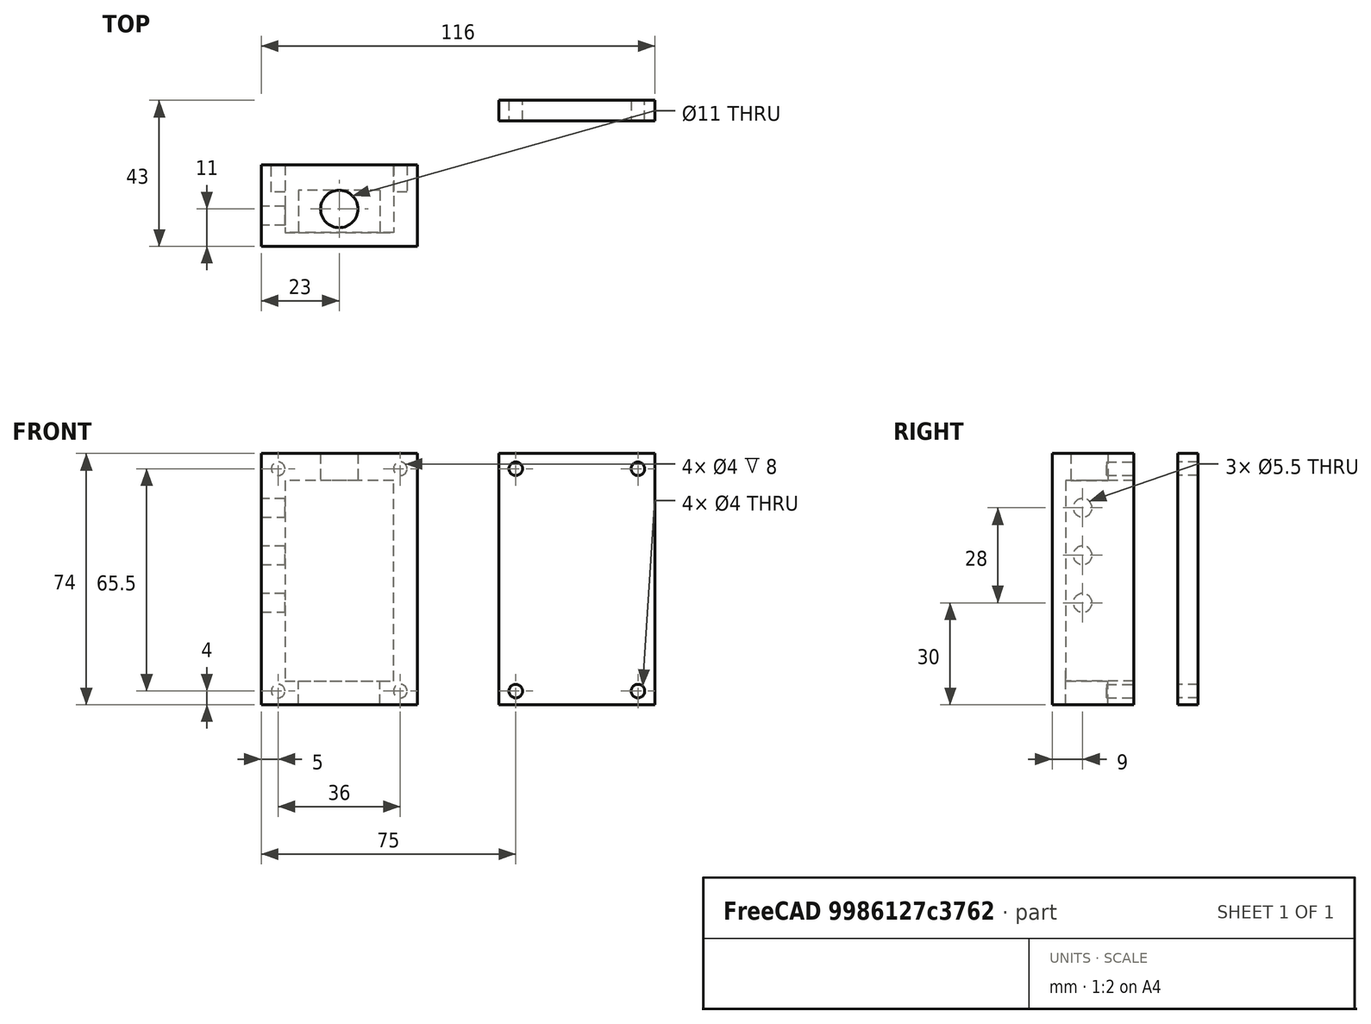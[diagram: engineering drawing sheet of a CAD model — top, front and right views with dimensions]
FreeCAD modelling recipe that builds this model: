
FCSTD DOCUMENT  (FreeCAD 0.20R29603 (Git))
Label: Reciever Housing
License: All rights reserved
LicenseURL: http://en.wikipedia.org/wiki/All_rights_reserved
objects: Sketcher::SketchObject×8, PartDesign::Pocket×5, PartDesign::Pad×2, PartDesign::Hole×2, Mesh::Feature×2, PartDesign::Body×2
note: 28 computed .brp shape members not serialized (recipe doc carries the construction recipe); baked Part::Feature solids carry a one-line shape summary decoded from their .brp

FEATURE [Sketcher::SketchObject] Sketch
  FullyConstrained = true
  MapMode = 5
  Placement = pos=(0,0,0) rot=(1,0,0;1.5708rad)
  Support = -> [XZ_Plane]
  sketch-geometry (4):
    g0: LineSegment StartX=-23 StartY=40 StartZ=0 EndX=23 EndY=40 EndZ=0
    g1: LineSegment StartX=23 StartY=40 StartZ=0 EndX=23 EndY=-34 EndZ=0
    g2: LineSegment StartX=23 StartY=-34 StartZ=0 EndX=-23 EndY=-34 EndZ=0
    g3: LineSegment StartX=-23 StartY=-34 StartZ=0 EndX=-23 EndY=40 EndZ=0
  constraints (12):
    c: Horizontal(g0)
    c: Vertical(g1)
    c: Horizontal(g2)
    c: Coincident(g1,g0)
    c: Coincident(g0,g3)
    c: Coincident(g1,g2)
    c: Coincident(g2,g3)
    c: DistanceX(g0,g0) = 46
    c: DistanceY(g1,g0) = 74
    c: DistanceX(g2,g1) = 46
    c: DistanceX(g-1,g1) = 23
    c: DistanceY(g1,g-1) = 34
FEATURE [PartDesign::Pad] Pad
  Direction = (0,-1,-2e-16)
  Length = 24
  Length2 = 10
  Placement = pos=(0,0,0) rot=(1,0,0;1.5708rad)
  Profile = -> Sketch
  ReferenceAxis = -> Sketch [N_Axis]
  Type = 0
FEATURE [Sketcher::SketchObject] Sketch001
  FullyConstrained = true
  MapMode = 5
  Placement = pos=(0,0,0) rot=(-1,0,0;1.5708rad)
  Support = -> [Pad]
  sketch-geometry (4):
    g0: LineSegment StartX=-16 StartY=27 StartZ=0 EndX=16 EndY=27 EndZ=0
    g1: LineSegment StartX=16 StartY=27 StartZ=0 EndX=16 EndY=-32 EndZ=0
    g2: LineSegment StartX=16 StartY=-32 StartZ=0 EndX=-16 EndY=-32 EndZ=0
    g3: LineSegment StartX=-16 StartY=-32 StartZ=0 EndX=-16 EndY=27 EndZ=0
  constraints (12):
    c: Horizontal(g0)
    c: Vertical(g1)
    c: Horizontal(g2)
    c: Vertical(g3)
    c: Coincident(g1,g0)
    c: Coincident(g0,g3)
    c: Coincident(g3,g2)
    c: Coincident(g1,g2)
    c: DistanceX(g0,g-1) = 16
    c: DistanceY(g-1,g0) = 27
    c: DistanceX(g0,g0) = 32
    c: DistanceY(g1,g0) = 59
FEATURE [PartDesign::Pocket] Pocket
  BaseFeature = -> Pad
  Direction = (0,-1,-2e-16)
  Length = 20
  Length2 = 5
  Placement = pos=(0,0,0) rot=(1,0,0;1.5708rad)
  Profile = -> Sketch001
  ReferenceAxis = -> Sketch001 [N_Axis]
  Type = 0
FEATURE [Sketcher::SketchObject] Sketch002  label="Power plug hole"
  FullyConstrained = true
  MapMode = 5
  Placement = pos=(0,0,40) rot=(0,0,1;3.14159rad)
  Support = -> [Pocket]
  sketch-geometry (1):
    g0: Circle CenterX=0 CenterY=13 CenterZ=0 NormalX=0 NormalY=0 NormalZ=1 AngleXU=0 Radius=5.5
  constraints (3):
    c: Diameter(g0) = 11
    c: DistanceX(g0,g-1) = 0
    c: DistanceY(g-1,g0) = 13
FEATURE [PartDesign::Hole] Hole
  BaseFeature = -> Pocket
  CustomThreadClearance = 0
  Depth = 25
  DepthType = 0
  Diameter = 6
  DrillForDepth = false
  DrillPoint = 1
  DrillPointAngle = 118
  HoleCutCountersinkAngle = 90
  HoleCutCustomValues = false
  HoleCutDepth = 0
  HoleCutDiameter = 6.1
  HoleCutType = 0
  ModelThread = false
  Placement = pos=(0,0,0) rot=(1,0,0;1.5708rad)
  Profile = -> Pocket [Face1]
  Tapered = false
  TaperedAngle = 90
  ThreadClass = 0
  ThreadDepth = 25
  ThreadDepthType = 0
  ThreadDirection = 0
  ThreadFit = 0
  ThreadSize = 0
  ThreadType = 0
  Threaded = false
  UseCustomThreadClearance = false
FEATURE [PartDesign::Hole] Hole001
  BaseFeature = -> Hole
  CustomThreadClearance = 0
  Depth = 25
  DepthType = 0
  Diameter = 11
  DrillForDepth = false
  DrillPoint = 1
  DrillPointAngle = 118
  HoleCutCountersinkAngle = 90
  HoleCutCustomValues = false
  HoleCutDepth = 0
  HoleCutDiameter = 6.1
  HoleCutType = 0
  ModelThread = false
  Placement = pos=(0,0,0) rot=(1,0,0;1.5708rad)
  Profile = -> Sketch002
  Tapered = false
  TaperedAngle = 90
  ThreadClass = 0
  ThreadDepth = 25
  ThreadDepthType = 0
  ThreadDirection = 0
  ThreadFit = 0
  ThreadSize = 0
  ThreadType = 0
  Threaded = false
  UseCustomThreadClearance = false
FEATURE [Mesh::Feature] JST_Female_3pin  label="JST Female 3pin"
  Placement = pos=(2e-16,-14,-47) rot=(0,-0.707107,0.707107;3.14159rad)
FEATURE [Sketcher::SketchObject] Sketch003  label="JST Connector Hole"
  FullyConstrained = true
  MapMode = 5
  Placement = pos=(0,0,-34) rot=(1,0,0;3.14159rad)
  Support = -> [Hole001]
  sketch-geometry (4):
    g0: LineSegment StartX=-12 StartY=20 StartZ=0 EndX=12 EndY=20 EndZ=0
    g1: LineSegment StartX=12 StartY=7.5 StartZ=0 EndX=12 EndY=20 EndZ=0
    g2: LineSegment StartX=12 StartY=7.5 StartZ=0 EndX=-12 EndY=7.5 EndZ=0
    g3: LineSegment StartX=-12 StartY=7.5 StartZ=0 EndX=-12 EndY=20 EndZ=0
  constraints (12):
    c: Horizontal(g0)
    c: Vertical(g1)
    c: Horizontal(g2)
    c: Vertical(g3)
    c: Coincident(g3,g0)
    c: Coincident(g0,g1)
    c: Coincident(g1,g2)
    c: Coincident(g2,g3)
    c: DistanceX(g-1,g1) = 12
    c: DistanceX(g2,g-1) = 12
    c: DistanceY(g2,g0) = 12.5
    c: DistanceY(g-1,g2) = 7.5
FEATURE [PartDesign::Pocket] Pocket001
  BaseFeature = -> Hole001
  Direction = (0,3e-16,1)
  Length = 10
  Length2 = 5
  Placement = pos=(0,0,0) rot=(1,0,0;1.5708rad)
  Profile = -> Sketch003
  ReferenceAxis = -> Sketch003 [N_Axis]
  Type = 0
FEATURE [Sketcher::SketchObject] Sketch004  label="Top"
  FullyConstrained = true
  MapMode = 5
  Placement = pos=(0,0,0) rot=(1,0,0;1.5708rad)
  Support = -> [XZ_Plane001]
  sketch-geometry (4):
    g0: LineSegment StartX=23 StartY=-34 StartZ=0 EndX=-23 EndY=-34 EndZ=0
    g1: LineSegment StartX=-23 StartY=-34 StartZ=0 EndX=-23 EndY=40 EndZ=0
    g2: LineSegment StartX=-23 StartY=40 StartZ=0 EndX=23 EndY=40 EndZ=0
    g3: LineSegment StartX=23 StartY=40 StartZ=0 EndX=23 EndY=-34 EndZ=0
  constraints (12):
    c: Horizontal(g0)
    c: Vertical(g1)
    c: Horizontal(g2)
    c: Vertical(g3)
    c: Coincident(g1,g2)
    c: Coincident(g3,g2)
    c: Coincident(g3,g0)
    c: Coincident(g1,g0)
    c: DistanceY(g0,g1) = 74
    c: DistanceX(g1,g2) = 46
    c: DistanceX(g0,g-1) = 23
    c: DistanceY(g0,g-1) = 34
FEATURE [PartDesign::Pad] Pad001
  Direction = (0,-1,-2e-16)
  Length = 6
  Length2 = 10
  Placement = pos=(0,0,0) rot=(1,0,0;1.5708rad)
  Profile = -> Sketch004
  ReferenceAxis = -> Sketch004 [N_Axis]
  Type = 0
FEATURE [Sketcher::SketchObject] Sketch005  label="TopMount Holes1"
  FullyConstrained = true
  MapMode = 5
  Placement = pos=(0,0,0) rot=(-1,0,0;1.5708rad)
  Support = -> [Pocket001]
  sketch-geometry (4):
    g0: Circle CenterX=18 CenterY=-35.5 CenterZ=0 NormalX=0 NormalY=0 NormalZ=1 AngleXU=0 Radius=2
    g1: Circle CenterX=-18 CenterY=-35.5 CenterZ=0 NormalX=0 NormalY=0 NormalZ=1 AngleXU=0 Radius=2
    g2: Circle CenterX=-18 CenterY=30 CenterZ=0 NormalX=0 NormalY=0 NormalZ=1 AngleXU=0 Radius=2
    g3: Circle CenterX=18 CenterY=30 CenterZ=0 NormalX=0 NormalY=0 NormalZ=1 AngleXU=0 Radius=2
  constraints (12):
    c: DistanceX(g-1,g0) = 18
    c: DistanceY(g0,g-1) = 35.5
    c: Diameter(g0) = 4
    c: DistanceY(g1,g-1) = 35.5
    c: DistanceX(g1,g-1) = 18
    c: Diameter(g1) = 4
    c: DistanceX(g2,g-1) = 18
    c: DistanceY(g-1,g2) = 30
    c: Diameter(g2) = 4
    c: DistanceX(g-1,g3) = 18
    c: DistanceY(g-1,g3) = 30
    c: Diameter(g3) = 4
FEATURE [PartDesign::Pocket] Pocket002
  BaseFeature = -> Pocket001
  Direction = (0,-1,2e-16)
  Length = 8
  Length2 = 5
  Placement = pos=(0,0,0) rot=(1,0,0;1.5708rad)
  Profile = -> Sketch005
  ReferenceAxis = -> Sketch005 [N_Axis]
  Type = 0
FEATURE [Sketcher::SketchObject] Sketch006  label="TopMount Holes2"
  FullyConstrained = true
  MapMode = 5
  Placement = pos=(0,-6,-1.3e-15) rot=(1,0,0;1.5708rad)
  Support = -> [Pad001]
  sketch-geometry (4):
    g0: Circle CenterX=-18 CenterY=35.5 CenterZ=0 NormalX=0 NormalY=0 NormalZ=1 AngleXU=0 Radius=2
    g1: Circle CenterX=18 CenterY=35.5 CenterZ=0 NormalX=0 NormalY=0 NormalZ=1 AngleXU=0 Radius=2
    g2: Circle CenterX=18 CenterY=-30 CenterZ=0 NormalX=0 NormalY=0 NormalZ=1 AngleXU=0 Radius=2
    g3: Circle CenterX=-18 CenterY=-30 CenterZ=0 NormalX=0 NormalY=0 NormalZ=1 AngleXU=0 Radius=2
  constraints (12):
    c: Diameter(g0) = 4
    c: Diameter(g1) = 4
    c: Diameter(g2) = 4
    c: Diameter(g3) = 4
    c: DistanceX(g0,g-1) = 18
    c: DistanceY(g-1,g0) = 35.5
    c: DistanceX(g-1,g1) = 18
    c: DistanceY(g-1,g1) = 35.5
    c: DistanceX(g3,g-1) = 18
    c: DistanceX(g-1,g2) = 18
    c: DistanceY(g3,g-1) = 30
    c: DistanceY(g2,g-1) = 30
FEATURE [PartDesign::Pocket] Pocket003
  BaseFeature = -> Pad001
  Direction = (0,1,2e-16)
  Length = 10
  Length2 = 5
  Placement = pos=(0,0,0) rot=(1,0,0;1.5708rad)
  Profile = -> Sketch006
  ReferenceAxis = -> Sketch006 [N_Axis]
  Type = 0
FEATURE [PartDesign::Body] Body001  label="Housing Top"
  Group = -> [Sketch004,Pad001,Sketch006,Pocket003]
  Origin = -> Origin001
  Placement = pos=(70,19,0) rot=(0,0,1;0rad)
  Tip = -> Pocket003
FEATURE [Sketcher::SketchObject] Sketch007  label="Status LED Holes"
  FullyConstrained = true
  MapMode = 5
  Placement = pos=(-23,0,0) rot=(0.707107,0,-0.707107;3.14159rad)
  Support = -> [Pocket002]
  sketch-geometry (3):
    g0: Circle CenterX=-24 CenterY=15 CenterZ=0 NormalX=0 NormalY=0 NormalZ=1 AngleXU=0 Radius=2.75
    g1: Circle CenterX=-10 CenterY=15 CenterZ=0 NormalX=0 NormalY=0 NormalZ=1 AngleXU=0 Radius=2.75
    g2: Circle CenterX=4 CenterY=15 CenterZ=0 NormalX=0 NormalY=0 NormalZ=1 AngleXU=0 Radius=2.75
  constraints (9):
    c: DistanceX(g0,g-1) = 24
    c: DistanceX(g1,g-1) = 10
    c: DistanceX(g2,g-1) = -4
    c: DistanceY(g-1,g0) = 15
    c: DistanceY(g-1,g1) = 15
    c: DistanceY(g-1,g2) = 15
    c: Diameter(g0) = 5.5
    c: Diameter(g1) = 5.5
    c: Diameter(g2) = 5.5
FEATURE [PartDesign::Pocket] Pocket004
  BaseFeature = -> Pocket002
  Direction = (1,0,2e-16)
  Length = 10
  Length2 = 5
  Placement = pos=(0,0,0) rot=(1,0,0;1.5708rad)
  Profile = -> Sketch007
  ReferenceAxis = -> Sketch007 [N_Axis]
  Type = 0
FEATURE [PartDesign::Body] Body  label="Housing Bottom"
  Group = -> [Sketch,Pad,Sketch001,Pocket,Hole,Sketch002,Hole001,Sketch003,Pocket001,Sketch005,Pocket002,Sketch007,Pocket004]
  Origin = -> Origin
  Tip = -> Pocket004
FEATURE [Mesh::Feature] Unnamed_Goouuu_ESP32_Development_Board001  label="ESP32_Development_Board"
  Placement = pos=(111,12,0) rot=(1,0,0;3.14159rad)
